AUTODESK INVENTOR PART (.ipt)
format: ipt  version: 2018 (Build 220112000, 112)  size: 84,480 bytes
history: native  units: mm
features: sketch x2, extrude x1
ambient origin geometry x8: Origin, YZ Plane, XZ Plane, XY Plane, X Axis, Y Axis, Z Axis, Center Point
bodies: Solid1 (feature_tree)
feature tree (3):
  extrude  "Extrusion1"  Depth=10.0mm
  sketch  "Sketch2"  dims[d2=3.5mm d3=0.0mm d4=0.5mm d5=1.0mm d6=2.0mm d7=3.0mm d8=3.5mm d9=2.0mm]
  sketch  "Sketch1"  dims[d0=3.5mm d1=10.0mm]
